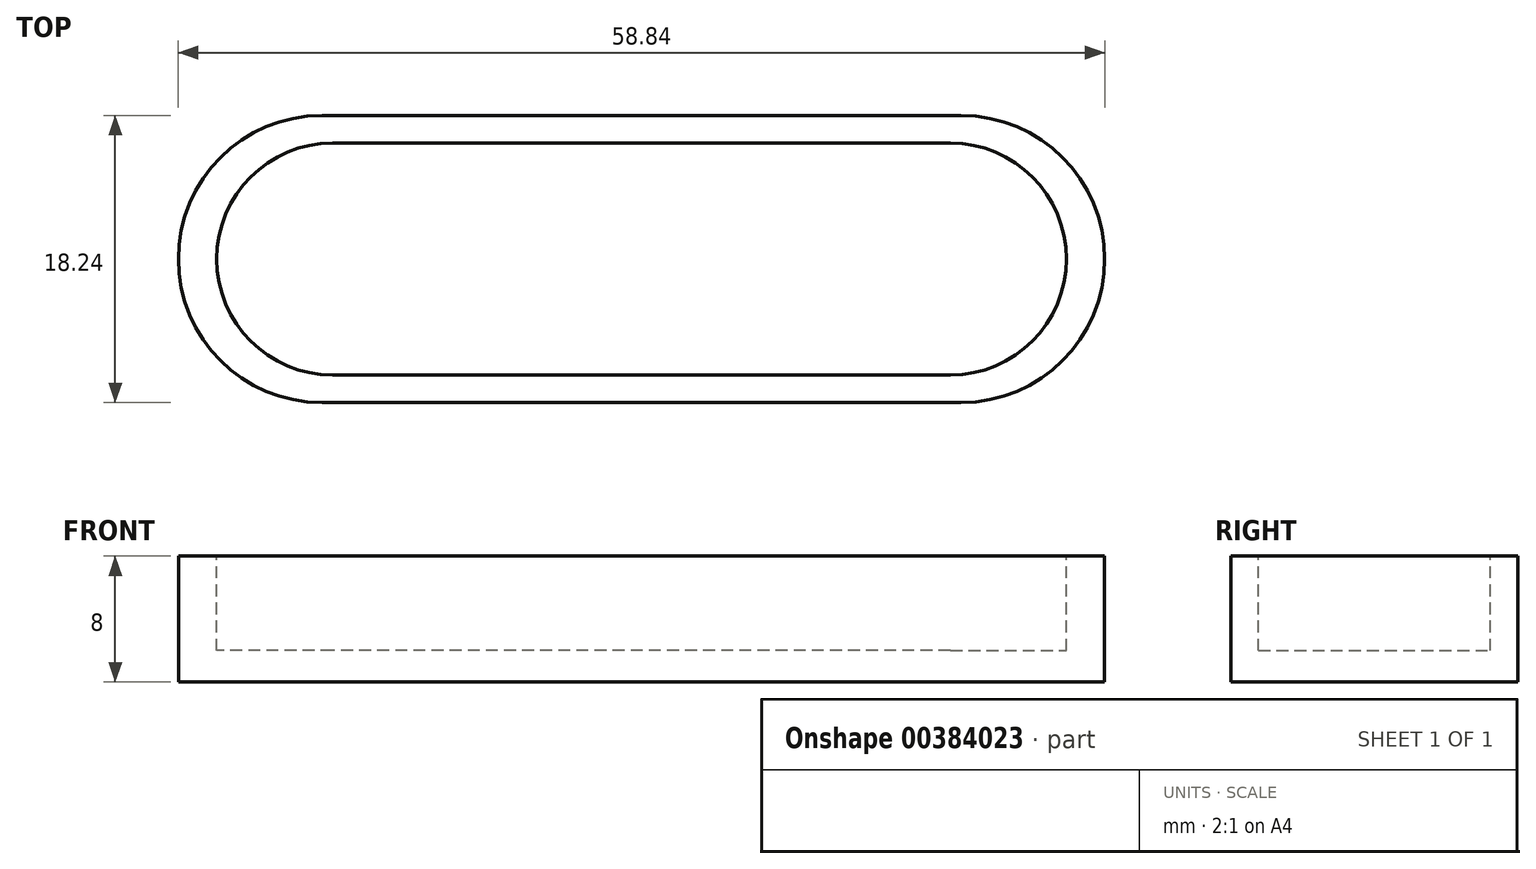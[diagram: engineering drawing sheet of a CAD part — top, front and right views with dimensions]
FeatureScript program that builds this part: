
annotation { "Feature Type Name" : "Feature", "Feature Type Description" : "" }
export const myFeature = defineFeature(function(context is Context, id is Id, definition is map)
    precondition{}
    {
        {
            var Q0;
            Q0=qCreatedBy(makeId("Top.planeOp"),FACE);
            var sketch = newSketch(context, id + "F0", { "sketchPlane" : qUnion([Q0])});
            skLineSegment(sketch, "E0.bottom", {"start": v(20.3, -9.12) * mm, "end": v(-20.3, -9.12) * mm});
            skLineSegment(sketch, "E0.top", {"start": v(20.3, 9.12) * mm, "end": v(-20.3, 9.12) * mm});
            skLineSegment(sketch, "E0.left", {"start": v(20.3, -9.12) * mm, "end": v(20.3, 9.12) * mm});
            skLineSegment(sketch, "E0.right", {"start": v(-20.3, -9.12) * mm, "end": v(-20.3, 9.12) * mm});
            skPoint(sketch, "E0.middle", {"position": v(0, 0) * mm});
            skArc(sketch, "E1", {"start": v(-20.3, 9.12) * mm, "mid": v(-29.42, 0) * mm, "end": v(-20.3, -9.12) * mm});
            skArc(sketch, "E2", {"start": v(20.3, -9.12) * mm, "mid": v(29.42, 0) * mm, "end": v(20.3, 9.12) * mm});
            skSolve(sketch);
        }
        {
            var Q0;
            Q0 = qSketchRegion(id + "F0", true);
            extrude(context, id + "F1", {"entities" : qUnion([Q0]), "depth" : 8 * mm});
        }
        {
            var Q0;
            Q0=makeQuery(id+"F1.opExtrude","CAP_FACE",FACE,{"disambiguationData":[OSD([sQuery(id+"F0.wireOp",EDGE,"E0.bottom"),sQuery(id+"F0.wireOp",EDGE,"E0.top"),sQuery(id+"F0.wireOp",EDGE,"E1"),sQuery(id+"F0.wireOp",EDGE,"E2")])],"isStart":false});
            var sketch = newSketch(context, id + "F2", { "sketchPlane" : qUnion([Q0])});
            skLineSegment(sketch, "E3.bottom", {"start": v(19.62, -7.36) * mm, "end": v(-19.62, -7.36) * mm});
            skLineSegment(sketch, "E3.top", {"start": v(19.62, 7.36) * mm, "end": v(-19.62, 7.36) * mm});
            skLineSegment(sketch, "E3.left", {"start": v(19.62, -7.36) * mm, "end": v(19.62, 7.36) * mm});
            skLineSegment(sketch, "E3.right", {"start": v(-19.62, -7.36) * mm, "end": v(-19.62, 7.36) * mm});
            skPoint(sketch, "E3.middle", {"position": v(0, 0) * mm});
            skArc(sketch, "E4", {"start": v(-19.62, 7.36) * mm, "mid": v(-26.98, 0) * mm, "end": v(-19.62, -7.36) * mm});
            skArc(sketch, "E5", {"start": v(19.62, -7.36) * mm, "mid": v(26.98, 0) * mm, "end": v(19.62, 7.36) * mm});
            skSolve(sketch);
        }
        {
            var Q0;
            Q0 = qSketchRegion(id + "F2", true);
            extrude(context, id + "F3", {"entities" : qUnion([Q0]), "operationType" : NewBodyOperationType.REMOVE, "oppositeDirection" : true, "depth" : 6 * mm});
        }
    });
